# Revit family: Brushed Stainless Steel #4
name_source: partatom
category: Specialty Equipment
units: mm (PartAtom-declared; Revit-internal decimal feet)

## family parameters
Always vertical = Yes
Cut with Voids When Loaded = No
OmniClass Number = 23.40.40.14.24.14
OmniClass Title = Service Line Equipment
Part Type = Normal
Room Calculation Point = No
Round Connector Dimension = Use Diameter
Shared = No
Work Plane-Based = Yes

## types (1)
- Brushed Stainless Steel #4
    Assembly Code = E1090320
    CSI MasterFormat = 11 46 16
    Default Elevation = 4' - 0"
    Depth = 1' - 8 1/2"
    Description = Food Shield
    Foodservice Equipment Identifier = Yes
    Frame Material = QF_Stainless-Brushed-Satin
    Height = 1' - 8 5/16"
    Identify Quantity as Lot = Yes
    KCL SpecSheet URL = http://kclweb.kclcad.com
    KCLRef = KCL2C9,,4fcd0080-62a8-4e9a-918e-6e877f88d02a,PB,FEM1R-G,638126942140000000,108bfd3f-0031-446b-af70-63a410cd73ef,664c4c62-2017-4f2f-ae4d-9081d051f00d
    Manufacturer = Premier Metal And Glass
    Masterspec = Division 11
    Model = FEM1R-G
    Specification by Manufacturer = 1Guard™ Fixed Self-Service Sneeze Guard, single sided guard, slanted front, tempered glass with polished edges, end 
panels, 1" OD round stainless supports, NSF (Contact Premier Sales Department for Pricing)
    URL = https://www.pmg-inc.com
    URL Cutsheet = https://www.pmg-inc.me
    Weight in Pounds = 0

## geometry (parser evidence)
native form markers: Sweep x57
no freeform markers — native parametric forms only
